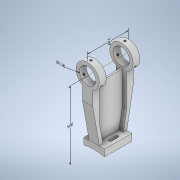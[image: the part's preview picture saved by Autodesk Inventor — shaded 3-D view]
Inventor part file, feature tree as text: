
AUTODESK INVENTOR PART (.ipt)
format: ipt  version: 2020.3 (Build 243373000, 373)  size: 3,553,280 bytes
history: native  units: in
note: dims shown in document units (in); Inventor stores cm internally (conversion verified against a paired STEP export)
features: sketch x20, extrude x8, thread x6, revolve x6, helix x6, other x5, plane x3, mirror x2, pattern_circular x1
ambient origin geometry x8: Origin, YZ Plane, XZ Plane, XY Plane, X Axis, Y Axis, Z Axis, Center Point
bodies: Solid1 (feature_tree), Solid3 (feature_tree), Solid4 (feature_tree), Solid5 (feature_tree), Solid6 (feature_tree), Solid7 (feature_tree), Solid8 (feature_tree)
feature tree (57):
  other  "Annotations"
  extrude  "Extrusion1"  Depth=0.75in
  extrude  "Extrusion2"  Depth=2.0in TaperAngle=0.0deg
  mirror  "Mirror1"
  extrude  "Extrusion3"  Depth=0.4in
  plane  "Work Plane1"
  extrude  "Extrusion4"  TaperAngle=0.0deg  [1 undecoded]
  extrude  "Extrusion5"  Depth=2.75in
  mirror  "Mirror4"
  extrude  "Extrusion6"  Depth=0.25in
  plane  "Work Plane3"
  extrude  "Extrusion7"  Depth=2.0in
  other  "Work Axis1"
  plane  "Work Plane4"
  extrude  "Extrusion9"  Depth=0.25in
  thread  "Thread2"  [1 undecoded]
  thread  "Thread3"  [1 undecoded]
  pattern_circular  "Circular Pattern1"  Count=3 Angle=360.0deg
  thread  "Thread4"  [1 undecoded]
  thread  "Thread5"  [1 undecoded]
  thread  "Thread6"  [1 undecoded]
  thread  "Thread7"  [1 undecoded]
  revolve  "Revolution2"  [1 undecoded]
  helix  "Coil2"  [1 undecoded]
  revolve  "Revolution3"  [1 undecoded]
  helix  "Coil3"  [1 undecoded]
  revolve  "Revolution4"  [1 undecoded]
  helix  "Coil4"  [1 undecoded]
  revolve  "Revolution5"  [1 undecoded]
  helix  "Coil5"  [1 undecoded]
  revolve  "Revolution6"  [1 undecoded]
  helix  "Coil6"  [1 undecoded]
  revolve  "Revolution7"  [1 undecoded]
  helix  "Coil7"  [1 undecoded]
  sketch  "Sketch1"  dims[d1=6.0in d2=0.75in]
  sketch  "Sketch2"  dims[d3=0.5in d4=2.0in d5=0.0in]
  sketch  "Sketch3"  dims[d6=0.0in d7=0.4in]
  sketch  "Sketch4"  dims[d8=0.25in d9=0.0in d10=0.0in]
  sketch  "Sketch7"  dims[d11=0.2in d13=2.75in]
  sketch  "Sketch8"  dims[d14=0.0687in d15=0.25in]
  sketch  "Sketch9"  dims[d16=0.75in d17=0.0in d18=2.0in]
  sketch  "Sketch14"  dims[d19=1.2in d20=0.25in d21=0.5in d22=0.0in d25=1.75in]
  sketch  "Sketch15"  dims[d26=0.75in d27=0.0in]
  sketch  "Sketch16"  dims[d31=0.75in d32=0.0in]
  sketch  "Sketch17"  dims[d38=0.125in d39=0.0in]
  sketch  "Sketch18"  dims[d62=0.0039in]
  sketch  "Sketch19"  dims[d64=60.0deg]
  sketch  "Sketch20"  dims[d74=0.159in]
  sketch  "Sketch21"  dims[d75=0.25in]
  sketch  "Sketch22"  dims[d76=0.25in]
  sketch  "Sketch23"  dims[d77=1.0in d78=0.0in]
  sketch  "Sketch24"  dims[d79=0.255in d80=0.0in]
  sketch  "Sketch25"  dims[d81=0.255in d82=0.0in d83=1.1811in d84=360.0deg d86=0.255in d87=0.0in d88=0.255in d89=0.0in d90=0.255in d91=0.0in d92=0.255in d93=0.0in]
  sketch  "Sketch26"  dims[d94=0.3779in d95=0.005in d96=0.005in d99=0.0312in d101=0.3779in d103=0.0in d104=0.0313in d105=0.3178in d106=0.3937in d107=0.0in d108=0.0in d109=0.0in d110=0.0in d111=0.0in d112=0.3779in d113=0.005in d114=0.005in d117=0.0312in d119=0.3779in d121=0.0in d122=0.0313in d123=0.3178in d124=0.3937in d125=0.0in d126=0.0in d127=0.0in d128=0.0in d129=0.0in d130=0.3779in d131=0.005in d132=0.005in d135=0.0312in d137=0.3779in d139=0.0in d140=0.0313in d141=0.3178in d142=0.3937in d143=0.0in d144=0.0in d145=0.0in d146=0.0in d147=0.0in d148=0.3779in d149=0.005in d150=0.005in d153=0.0312in d155=0.3779in d157=0.0in d158=0.0313in d159=0.3178in d160=0.3937in d161=0.0in d162=0.0in d163=0.0in d164=0.0in d165=0.0in d166=0.3779in d167=0.005in d168=0.005in d171=0.0312in d173=0.3779in d175=0.0in d176=0.0313in d177=0.3178in d178=0.3937in d179=0.0in d180=0.0in d181=0.0in d182=0.0in d183=0.0in d184=0.3779in d185=0.005in d186=0.005in d189=0.0312in d191=0.3779in d193=0.0in d194=0.0313in d195=0.3178in d196=0.3937in d197=0.0in d198=0.0in d199=0.0in d200=0.0in d201=0.0in d33=-0.1818in d34=5.0in d35=2.9698in d36=1.1814in d37=1.2in d28=0.5in d29=0.0344in]
  other  "Linear Dimension 1"
  other  "Linear Dimension 2"
  other  "Diameter Dimension 1"
note: 19 required parameter values undecoded (feature->parameter linkage not recoverable at this tier; creation-order binding heuristic only, values carry confidence <= 0.55)